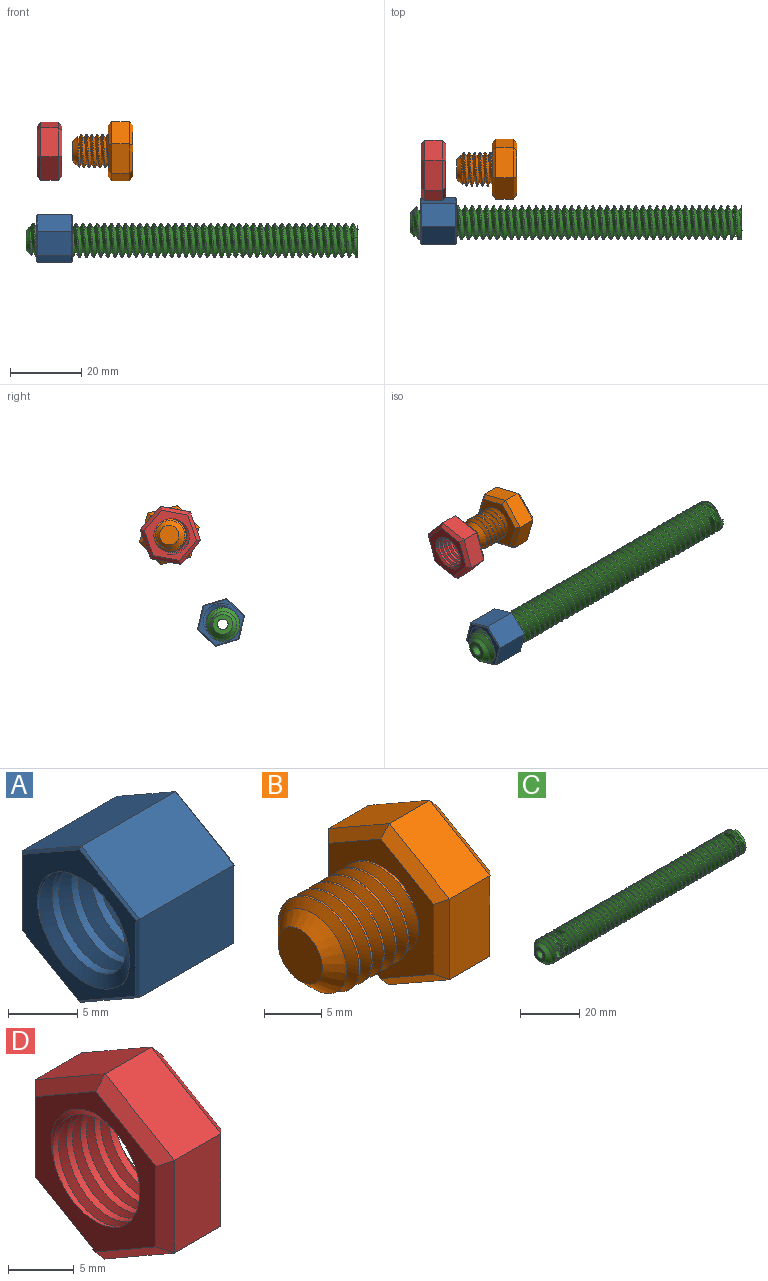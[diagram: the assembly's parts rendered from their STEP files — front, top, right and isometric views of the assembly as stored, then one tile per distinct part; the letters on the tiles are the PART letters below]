
ASSEMBLY  parts=4 mates=2
PART A: 23 faces, bbox 12.3x13x14.5 mm
  f0: cylinder r=4.25mm len=10mm, axis (1,0,0), area 93.9mm2, adj f7,f8,f21,f22
  f1: plane 9.6x5.98mm, normal (0,-0.5,0.86), area 66.5mm2, adj f2,f6,f14,f18
  f2: plane 9.6x6.93mm, normal (0,-1,-0.01), area 66.5mm2, adj f1,f3,f12,f16
  f3: plane 9.6x6.02mm, normal (0,-0.5,-0.87), area 66.5mm2, adj f2,f4,f10,f15
  f4: plane 9.6x5.98mm, normal (0,0.5,-0.86), area 66.5mm2, adj f3,f5,f9,f17
  f5: plane 9.6x6.93mm, normal (0,1,0.01), area 66.5mm2, adj f4,f6,f11,f19
  f6: plane 9.6x6.02mm, normal (0,0.5,0.87), area 66.5mm2, adj f1,f5,f13,f20
  f7: plane 14x12.24mm, normal (-1,0,0), area 49.2mm2, adj f0,f9,f10,f11,f12,f13,f14,f21
  f8: plane 14x12.24mm, normal (1,0,0), area 49.2mm2, adj f0,f15,f16,f17,f18,f19,f20,f21
  f9: plane 5.98x3.61mm, normal (-0.71,0.36,-0.61), area 1.9mm2, adj f4,f7,f10,f11
  f10: plane 6.02x3.55mm, normal (-0.71,-0.35,-0.61), area 1.9mm2, adj f3,f7,f9,f12
  f11: plane 6.93x0.23mm, normal (-0.71,0.71,0), area 1.9mm2, adj f5,f7,f9,f13
  f12: plane 6.93x0.23mm, normal (-0.71,-0.71,0), area 1.9mm2, adj f2,f7,f10,f14
  f13: plane 6.02x3.55mm, normal (-0.71,0.35,0.61), area 1.9mm2, adj f6,f7,f11,f14
  f14: plane 5.98x3.61mm, normal (-0.71,-0.36,0.61), area 1.9mm2, adj f1,f7,f12,f13
  f15: plane 6.02x3.55mm, normal (0.71,-0.35,-0.61), area 1.9mm2, adj f3,f8,f16,f17
  f16: plane 6.93x0.23mm, normal (0.71,-0.71,0), area 1.9mm2, adj f2,f8,f15,f18
  f17: plane 5.98x3.61mm, normal (0.71,0.36,-0.61), area 1.9mm2, adj f4,f8,f15,f19
  f18: plane 5.98x3.61mm, normal (0.71,-0.36,0.61), area 1.9mm2, adj f1,f8,f16,f20
  f19: plane 6.93x0.23mm, normal (0.71,0.71,0), area 1.9mm2, adj f5,f8,f17,f20
  f20: plane 6.02x3.55mm, normal (0.71,0.35,0.61), area 1.9mm2, adj f6,f8,f18,f19
  f21: bspline ~12.41x11.65mm, area 196.6mm2, adj f0,f7,f8,f22
  f22: bspline ~12.41x11.32mm, area 196.5mm2, adj f0,f7,f8,f21
PART B: 25 faces, bbox 17.8x15.9x18.1 mm
  f0: cylinder r=4.75mm len=9.5mm, axis (1,0,0), area 28.1mm2, adj f1,f2,f4,f12
  f1: bspline ~10.97x9.91mm, area 196.7mm2, adj f0,f2,f4,f12
  f2: bspline ~10.97x10.66mm, area 196.6mm2, adj f0,f1,f4,f12
  f3: plane 5.5x5.5mm, normal (-1,0,0), area 23.8mm2, adj f4
  f4: cone r=4.75mm half-angle=45deg, axis (1,0,0), area 47.4mm2, adj f0,f1,f2,f3
  f5: plane 7.48x5mm, normal (0,-0.5,0.86), area 43.3mm2, adj f6,f10,f18,f22
  f6: plane 8.66x5mm, normal (0,-1,0), area 43.3mm2, adj f5,f7,f16,f20
  f7: plane 7.52x5mm, normal (0,-0.5,-0.87), area 43.3mm2, adj f6,f8,f14,f19
  f8: plane 7.48x5mm, normal (0,0.5,-0.86), area 43.3mm2, adj f7,f9,f13,f21
  f9: plane 8.66x5mm, normal (0,1,0), area 43.3mm2, adj f8,f10,f15,f23
  f10: plane 7.52x5mm, normal (0,0.5,0.87), area 43.3mm2, adj f5,f9,f17,f24
  f11: plane 15.01x13.03mm, normal (1,0,0), area 146.4mm2, adj f13,f14,f15,f16,f17,f18
  f12: plane 15.83x13.85mm, normal (-1,0,0), area 89.2mm2, adj f0,f1,f2,f19,f20,f21,f22,f23
  f13: plane 7.49x4.93mm, normal (0.71,0.36,-0.61), area 11.4mm2, adj f8,f11,f14,f15
  f14: plane 7.52x4.88mm, normal (0.71,-0.35,-0.61), area 11.4mm2, adj f7,f11,f13,f16
  f15: plane 8.66x1.03mm, normal (0.71,0.71,0), area 11.4mm2, adj f9,f11,f13,f17
  f16: plane 8.66x1.03mm, normal (0.71,-0.71,0), area 11.4mm2, adj f6,f11,f14,f18
  f17: plane 7.52x4.88mm, normal (0.71,0.35,0.61), area 11.4mm2, adj f10,f11,f15,f18
  f18: plane 7.49x4.93mm, normal (0.71,-0.36,0.61), area 11.4mm2, adj f5,f11,f16,f17
  f19: plane 7.52x4.88mm, normal (-0.71,-0.35,-0.61), area 11.4mm2, adj f7,f12,f20,f21
  f20: plane 8.66x1.03mm, normal (-0.71,-0.71,0), area 11.4mm2, adj f6,f12,f19,f22
  f21: plane 7.49x4.93mm, normal (-0.71,0.36,-0.61), area 11.4mm2, adj f8,f12,f19,f23
  f22: plane 7.49x4.93mm, normal (-0.71,-0.36,0.61), area 11.4mm2, adj f5,f12,f20,f24
  f23: plane 8.66x1.03mm, normal (-0.71,0.71,0), area 11.4mm2, adj f9,f12,f21,f24
  f24: plane 7.52x4.88mm, normal (-0.71,0.35,0.61), area 11.4mm2, adj f10,f12,f22,f23
PART C: 19 faces, bbox 96.2x12.2x10.7 mm
  f0: cylinder r=4.8mm len=9.6mm, axis (1,0,0), area 7.2mm2, adj f3,f5,f12,f18
  f1: cylinder r=4.8mm len=87.54mm, axis (1,0,0), area 45.2mm2, adj f10,f13,f14,f15,f18
  f2: cylinder r=4.8mm len=9.24mm, axis (1,0,0), area 3.1mm2, adj f3,f6,f17,f18
  f3: bspline ~11.09x9.6mm, area 67mm2, adj f0,f2,f5,f12,f17,f18
  f4: bspline ~11.09x7.2mm, area 17.2mm2, adj f5,f8,f17,f18
  f5: bspline ~11.09x9.6mm, area 68.2mm2, adj f0,f3,f4,f11,f12,f17,f18
  f6: bspline ~11.09x7.2mm, area 17.2mm2, adj f2,f14,f17,f18
  f7: cylinder r=1.5mm len=5mm, axis (-1,0,0), area 38.1mm2, adj f9,f17,f18
  f8: cylinder r=4.8mm len=9.24mm, axis (1,0,0), area 3.1mm2, adj f4,f15,f17,f18
  f9: plane 5.6x5.6mm, normal (-1,0,0), area 17.6mm2, adj f7,f11
  f10: plane 10.68x10.07mm, normal (1,0,0), area 56.4mm2, adj f1,f13,f14,f16
  f11: cone r=4.8mm half-angle=45deg, axis (1,0,0), area 34.3mm2, adj f5,f9,f12
  f12: cone r=4.8mm half-angle=45deg, axis (1,0,0), area 7.9mm2, adj f0,f3,f5,f11
  f13: plane 1.52x0.88mm, normal (0,1,0), area 0.7mm2, adj f1,f10,f15
  f14: bspline ~89.54x11.09mm, area 1947mm2, adj f1,f6,f10,f15,f17,f18
  f15: bspline ~88.54x11.09mm, area 1949.7mm2, adj f1,f8,f13,f14,f17,f18
  f16: cylinder r=1.5mm len=88.5mm, axis (-1,0,0), area 825.1mm2, adj f10,f17,f18
  f17: cylinder r=1.5mm len=4.57mm, axis (0,-1,0), area 27.1mm2, adj f2,f3,f4,f5,f6,f7,f8,f14
  f18: cylinder r=1.5mm len=4.71mm, axis (0,-1,0), area 30.2mm2, adj f0,f1,f2,f3,f4,f5,f6,f7
PART D: 23 faces, bbox 9.1x15.4x17.7 mm
  f0: plane 7.49x5mm, normal (0,-0.5,0.86), area 43.3mm2, adj f1,f5,f13,f17
  f1: plane 8.66x5mm, normal (0,-1,0), area 43.3mm2, adj f0,f2,f11,f15
  f2: plane 7.51x5mm, normal (0,-0.5,-0.87), area 43.3mm2, adj f1,f3,f9,f14
  f3: plane 7.49x5mm, normal (0,0.5,-0.86), area 43.3mm2, adj f2,f4,f8,f16
  f4: plane 8.66x5mm, normal (0,1,0), area 43.3mm2, adj f3,f5,f10,f18
  f5: plane 7.51x5mm, normal (0,0.5,0.87), area 43.3mm2, adj f0,f4,f12,f19
  f6: plane 15.37x13.38mm, normal (-1,0,0), area 71.4mm2, adj f8,f9,f10,f11,f12,f13,f20,f21
  f7: plane 15.37x13.38mm, normal (1,0,0), area 71.4mm2, adj f14,f15,f16,f17,f18,f19,f20,f21
  f8: plane 7.49x4.93mm, normal (-0.71,0.36,-0.61), area 11.4mm2, adj f3,f6,f9,f10
  f9: plane 7.51x4.89mm, normal (-0.71,-0.35,-0.61), area 11.4mm2, adj f2,f6,f8,f11
  f10: plane 8.66x1.02mm, normal (-0.71,0.71,0), area 11.4mm2, adj f4,f6,f8,f12
  f11: plane 8.66x1.02mm, normal (-0.71,-0.71,0), area 11.4mm2, adj f1,f6,f9,f13
  f12: plane 7.51x4.89mm, normal (-0.71,0.35,0.61), area 11.4mm2, adj f5,f6,f10,f13
  f13: plane 7.49x4.93mm, normal (-0.71,-0.36,0.61), area 11.4mm2, adj f0,f6,f11,f12
  f14: plane 7.51x4.89mm, normal (0.71,-0.35,-0.61), area 11.4mm2, adj f2,f7,f15,f16
  f15: plane 8.66x1.02mm, normal (0.71,-0.71,0), area 11.4mm2, adj f1,f7,f14,f17
  f16: plane 7.49x4.93mm, normal (0.71,0.36,-0.61), area 11.4mm2, adj f3,f7,f14,f18
  f17: plane 7.49x4.93mm, normal (0.71,-0.36,0.61), area 11.4mm2, adj f0,f7,f15,f19
  f18: plane 8.66x1.02mm, normal (0.71,0.71,0), area 11.4mm2, adj f4,f7,f16,f19
  f19: plane 7.51x4.89mm, normal (0.71,0.35,0.61), area 11.4mm2, adj f5,f7,f17,f18
  f20: cylinder r=4.66mm len=9.32mm, axis (1,0,0), area 85.4mm2, adj f6,f7,f21,f22
  f21: bspline ~12.5x10.82mm, area 128.4mm2, adj f6,f7,f20,f22
  f22: bspline ~12.5x10.82mm, area 128.5mm2, adj f6,f7,f20,f21
PLACE A rot(axis=(0,0.6,-0.8),180deg) t=(-55.27,-6.86,23.48)mm fixed
PLACE B rot(axis=(-1,0,0),43.8deg) t=(-31.66,7.73,48.08)mm
PLACE C rot(axis=(1,0,0),81.1deg) t=(35.23,-7.35,22.96)mm
PLACE D rot(axis=(1,0,0),100.2deg) t=(-48.16,7.38,48.02)mm fixed
MATE cylindrical C.f0 <-> A.f7  axis (-1,0,0) through (-58.27,-7.35,22.96)mm
MATE cylindrical B.f0 <-> D.f6  axis (-1,0,0) through (-45.16,7.73,48.08)mm
